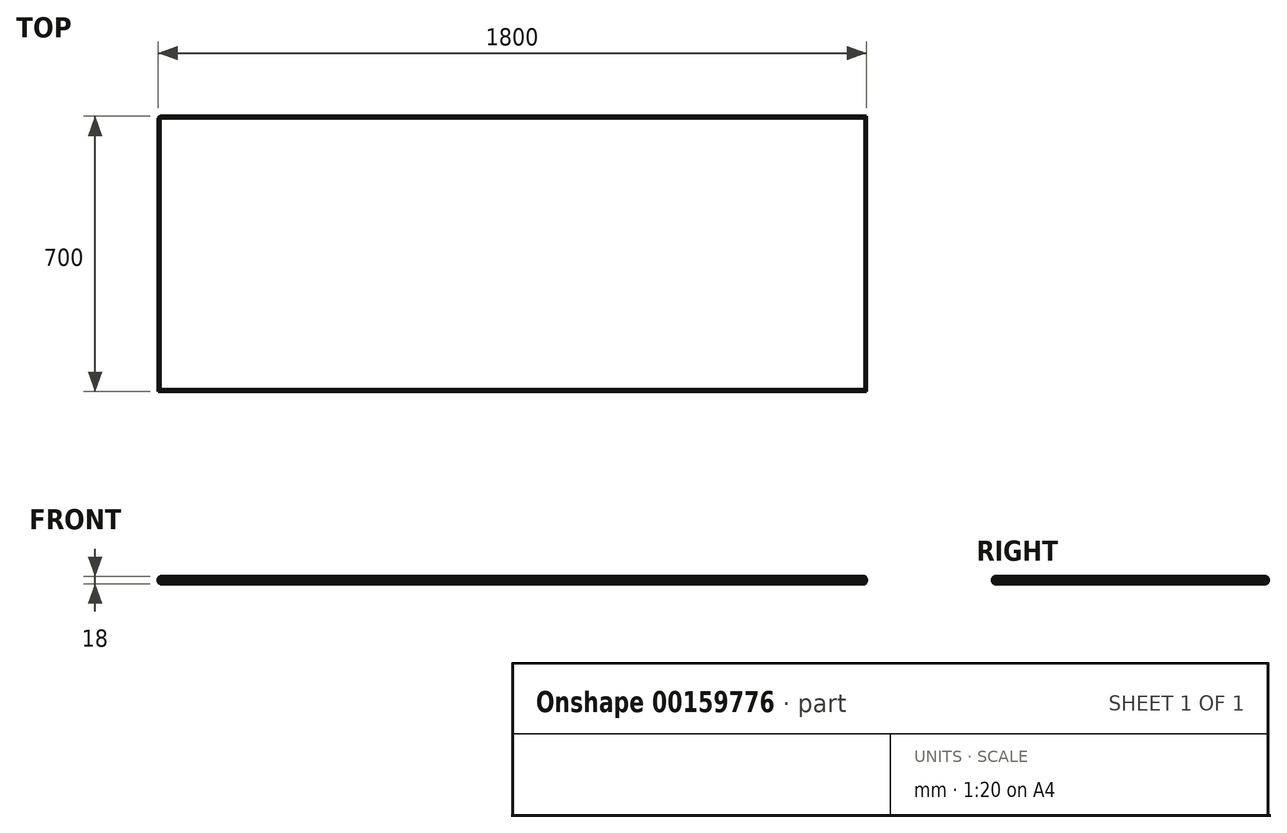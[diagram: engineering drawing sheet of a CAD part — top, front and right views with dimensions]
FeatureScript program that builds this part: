
annotation { "Feature Type Name" : "Feature", "Feature Type Description" : "" }
export const myFeature = defineFeature(function(context is Context, id is Id, definition is map)
    precondition{}
    {
        {
            var Q0;
            Q0=qCreatedBy(makeId("Top.planeOp"),FACE);
            var sketch = newSketch(context, id + "F0", { "sketchPlane" : qUnion([Q0])});
            skLineSegment(sketch, "E0.bottom", {"start": v(900, 350) * mm, "end": v(-900, 350) * mm});
            skLineSegment(sketch, "E0.top", {"start": v(900, -350) * mm, "end": v(-900, -350) * mm});
            skLineSegment(sketch, "E0.left", {"start": v(900, 350) * mm, "end": v(900, -350) * mm});
            skLineSegment(sketch, "E0.right", {"start": v(-900, 350) * mm, "end": v(-900, -350) * mm});
            skPoint(sketch, "E0.middle", {"position": v(0, 0) * mm});
            skSolve(sketch);
        }
        {
            var Q0;
            Q0 = qSketchRegion(id + "F0", true);
            extrude(context, id + "F1", {"entities" : qUnion([Q0]), "depth" : 18 * mm});
        }
        {
            var Q0;
            Q0=makeQuery(id+"F1.opExtrude","CAP_FACE",FACE,{"disambiguationData":[OSD([sQuery(id+"F0.wireOp",EDGE,"E0.bottom"),sQuery(id+"F0.wireOp",EDGE,"E0.top"),sQuery(id+"F0.wireOp",EDGE,"E0.left"),sQuery(id+"F0.wireOp",EDGE,"E0.right")])],"isStart":false});
            var Q1;
            Q1=makeQuery(id+"F1.opExtrude","CAP_FACE",FACE,{"disambiguationData":[OSD([sQuery(id+"F0.wireOp",EDGE,"E0.bottom"),sQuery(id+"F0.wireOp",EDGE,"E0.top"),sQuery(id+"F0.wireOp",EDGE,"E0.left"),sQuery(id+"F0.wireOp",EDGE,"E0.right")])],"isStart":true});
            chamfer(context, id + "F2", {"entities" : qUnion([Q0, Q1]), "width" : 5 * mm, "tangentPropagation" : true});
        }
        {
            var Q0;
            Q0=makeQuery(id+"F1.opExtrude","SWEPT_EDGE",EDGE,{"disambiguationData":[OSD([sQuery(id+"F0.wireOp",EDGE,"E0.bottom"),sQuery(id+"F0.wireOp",EDGE,"E0.right")])]});
            chamfer(context, id + "F3", {"entities" : qUnion([Q0]), "width" : 5 * mm, "tangentPropagation" : true});
        }
    });
